# Revit family: Cortadora_CK-38V_1_GENERADO
name_source: partatom
category: Equipos especializados
revit_build: Autodesk Revit 2016 (Build: 20151007_0715(x64)
units: mm (PartAtom-declared; Revit-internal decimal feet)

## family parameters
Compartido = No
Corte con vacíos al cargar = No
Cota de conector redondo = Diámetro de uso
Número OmniClass = 23.21.21.31.15
Punto de cálculo de habitación = No
Se basa en plano de trabajo = No
Siempre vertical = Sí
Tipo de pieza = Normal

## types (4) — shared parameters
Comentarios de tipo = 2 in 1: vegetable cutter (450 kg/h) + cutter with 8 litre bowl.
Depth = 409 mm  [stored 1.34186 ft]
Fabricante = SAMMIC S.L.
Foodservice Equipment Identifier = Sí
Height = 552 mm  [stored 1.81102 ft]
Revision Code = 1
Specification by Manufacturer = It has a variable speed motor block, universal head and 8-lt cutter bowl equipped with a rotor with micro-serrated blades.
Brushless technology.
URL = https://www.sammic.com
URL Cutsheet = http://www.sammic.com
Weight in Pounds = 60.8
Width = 391 mm  [stored 1.28281 ft]

## per-type parameters (varying)
| type | Conn Plug | Cycle | FL Amps | HP | Modelo | Phase | Volts | Watts |
| Combi vegetable prep.-cutter CK-38V 230/50-60/1 | EU (SCHUKO 2P+G) | 50 Hz | 10 A | 2.01 | 1050808 | 1 | 230 V | 1500 W |
| Combi vegetable prep.-cutter CK-38V 120/50-60/1 | USA (NEMA 5-15P / 2P+G) | 60 Hz | 15 A | 2.95 | 1050809 | 1 | 120 V | 2200 W |
| Combi vegetable prep.-cutter CK-38V 230/50-60/1 AUS | AU/NZ (AS 3112 10A / 2P) | 50 Hz | 10 A | 2.01 | 1050810 | 1 | 230 V | 1500 W |
| Combi vegetable prep.-cutter CK-38V 230/50-60/1 K | EU (SCHUKO 2P+G) | 0 Hz | 0 A | 2.01 | 1050812 | 0 | 0 V | 1500 W |

note: column(s) folded — value = type name in every type: Descripción

note: [stored X ft] marks values corroborated as IEEE doubles in the binary element streams (Revit-internal decimal feet)
